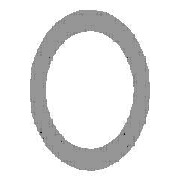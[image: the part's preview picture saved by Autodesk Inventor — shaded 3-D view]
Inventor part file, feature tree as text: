
AUTODESK INVENTOR PART (.ipt)
format: ipt  version: 2013 (Build 170138000, 138)  size: 108,544 bytes
history: native  units: mm (DEFAULTED — no unit token found)
features: other x4, sketch x3, plane x1
ambient origin geometry x8: Origin, YZ Plane, XZ Plane, XY Plane, X Axis, Y Axis, Z Axis, Center Point
bodies: Solid1 (feature_tree), Body (feature_tree)
feature tree (8):
  parser-record x1  (decoder bookkeeping rows leaked as tree rows — omitted from the tree; the rows remain in map.json)
  other  "Driven Length"
  other  "Start plane"
  other  "End plane"
  sketch  "Sketch"  dims[d2=508.0mm d3=0.0mm d4=-0.0mm d5=508.0mm d6=90.0deg d7=508.0mm]
  sketch  "Sketch3"  dims[d0=33.401mm]
  plane  "Work Plane3"
  sketch  "Sketch4"  dims[d1=3.3782mm]
